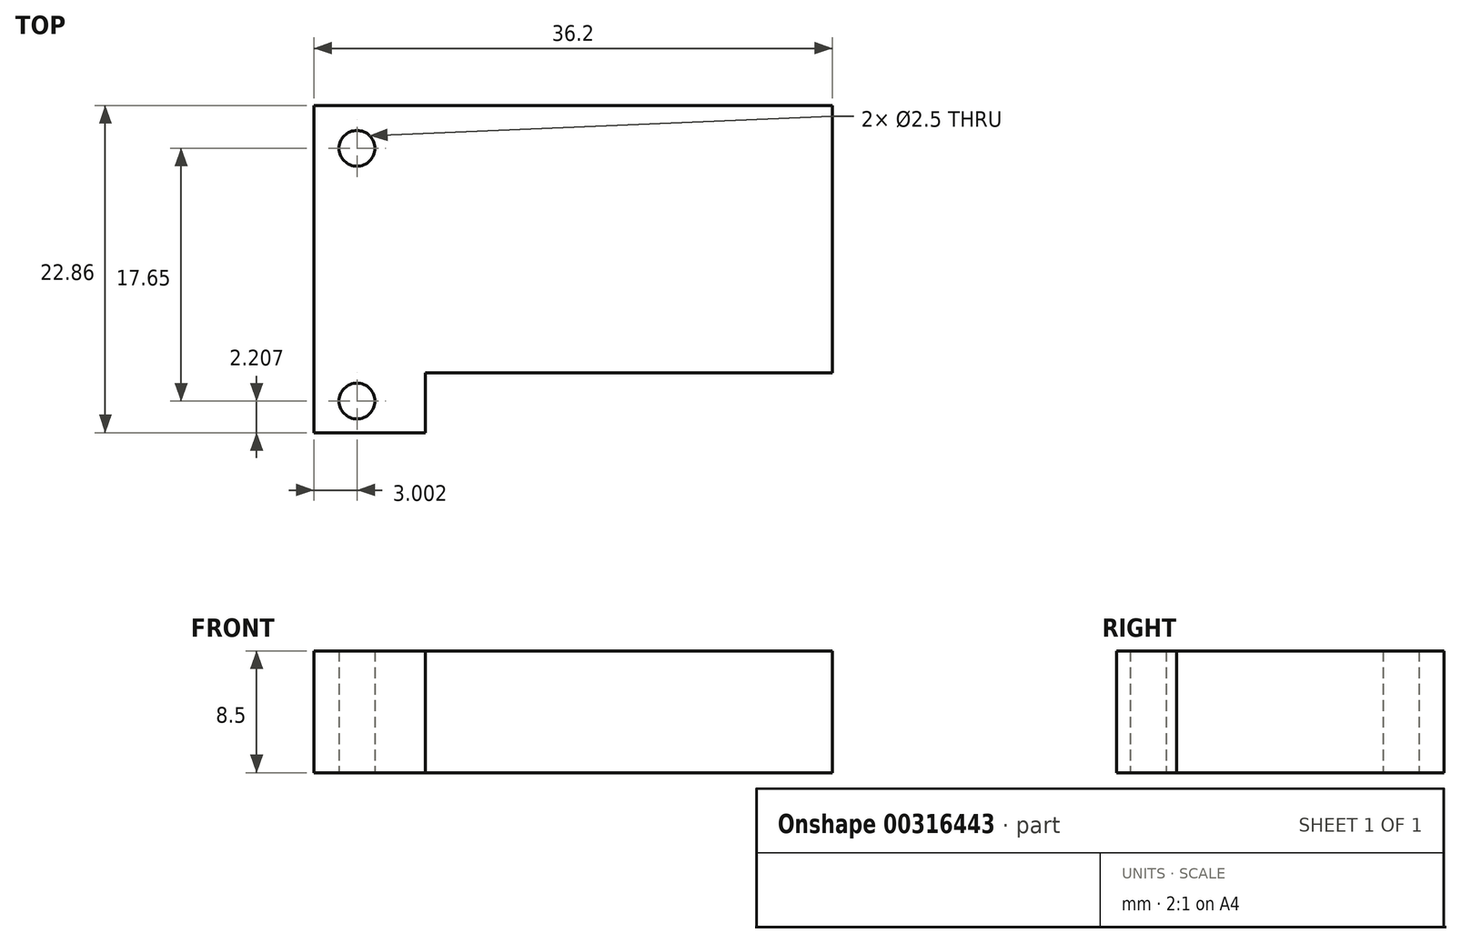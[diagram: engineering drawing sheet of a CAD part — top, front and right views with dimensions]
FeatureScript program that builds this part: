
annotation { "Feature Type Name" : "Feature", "Feature Type Description" : "" }
export const myFeature = defineFeature(function(context is Context, id is Id, definition is map)
    precondition{}
    {
        {
            var Q0;
            Q0=qCreatedBy(makeId("Top.planeOp"),FACE);
            var sketch = newSketch(context, id + "F0", { "sketchPlane" : qUnion([Q0])});
            skCircle(sketch, "E0", {"center": v(-38.18, 34.43) * mm, "radius": 1.25 * mm});
            skCircle(sketch, "E1", {"center": v(-38.18, 16.78) * mm, "radius": 1.25 * mm});
            skLineSegment(sketch, "E2.bottom", {"start": v(-41.18, 37.43) * mm, "end": v(-4.98, 37.43) * mm});
            skLineSegment(sketch, "E2.left", {"start": v(-41.18, 37.43) * mm, "end": v(-41.18, 14.57) * mm});
            skLineSegment(sketch, "E2.right", {"start": v(-4.98, 37.43) * mm, "end": v(-4.98, 18.75) * mm});
            skLineSegment(sketch, "E3", {"start": v(-41.18, 14.57) * mm, "end": v(-33.39, 14.57) * mm});
            skLineSegment(sketch, "E4", {"start": v(-33.39, 14.57) * mm, "end": v(-33.39, 18.75) * mm});
            skLineSegment(sketch, "E5", {"start": v(-33.39, 18.75) * mm, "end": v(-4.98, 18.75) * mm});
            skSolve(sketch);
        }
        {
            var Q0;
            Q0=makeQuery(id+"F0.imprint","IMPRINT",FACE,{"disambiguationData":[TD([[makeQuery(id+"F0.imprint","IMPRINT",EDGE,{"derivedFrom":sQuery(id+"F0.wireOp",EDGE,"E0")}),-1.0]])]});
            extrude(context, id + "F1", {"entities" : qUnion([Q0]), "depth" : 8.5 * mm, "offsetDistance" : 25 * mm});
        }
    });
